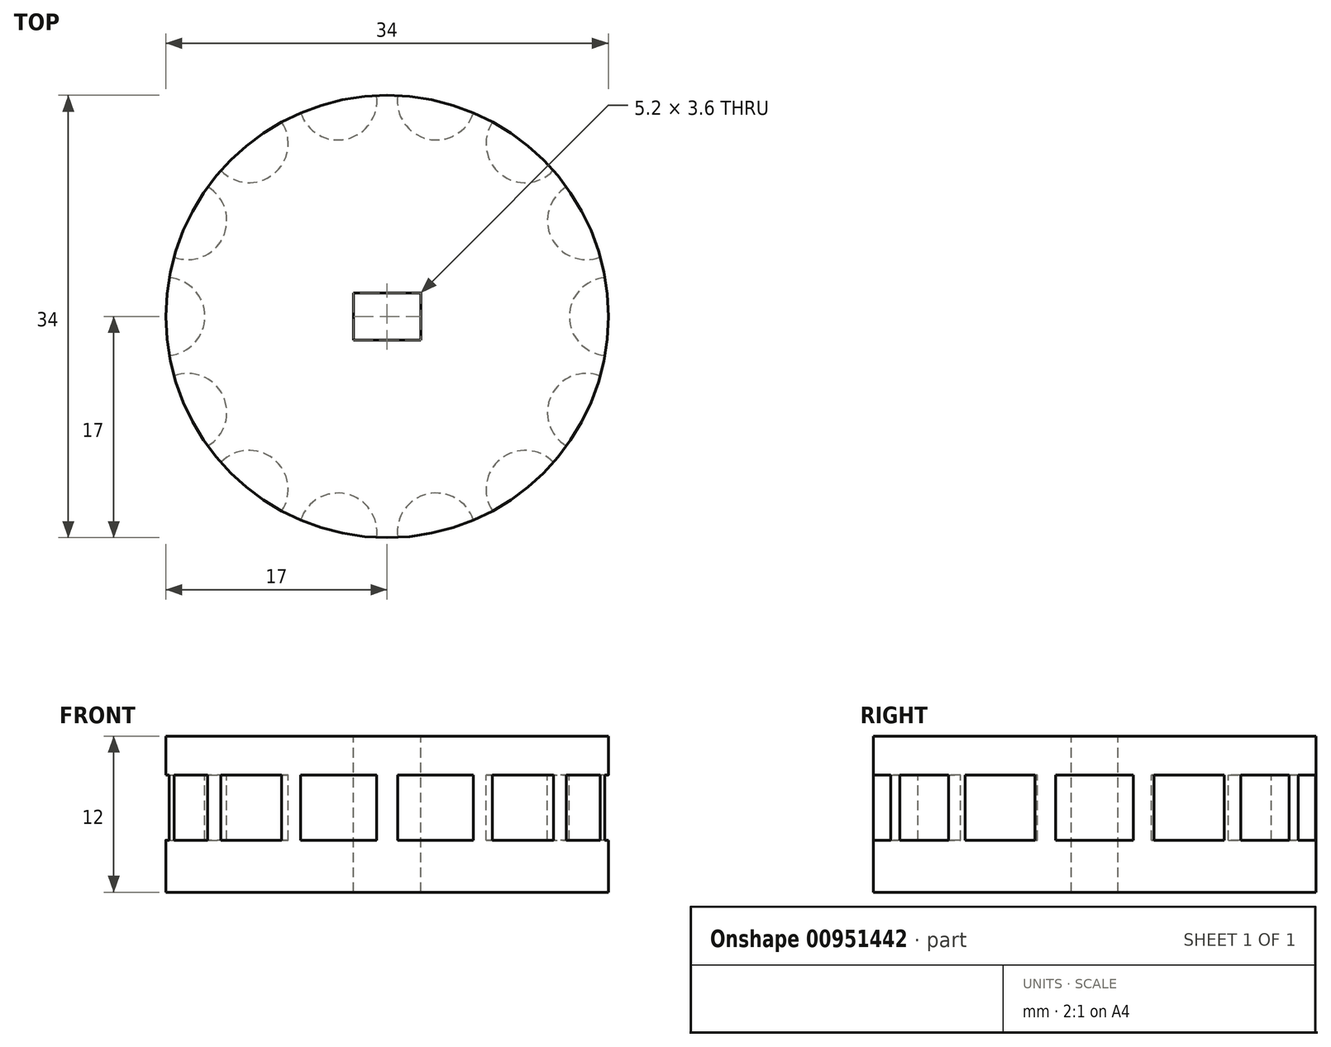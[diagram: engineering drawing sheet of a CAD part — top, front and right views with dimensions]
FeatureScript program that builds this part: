
annotation { "Feature Type Name" : "Feature", "Feature Type Description" : "" }
export const myFeature = defineFeature(function(context is Context, id is Id, definition is map)
    precondition{}
    {
        {
            var Q0;
            Q0=qCreatedBy(makeId("Top.planeOp"),FACE);
            var sketch = newSketch(context, id + "F0", { "sketchPlane" : qUnion([Q0])});
            skCircle(sketch, "E0", {"center": v(0, 0) * mm, "radius": 17 * mm});
            skSolve(sketch);
        }
        {
            var Q0;
            Q0=makeQuery(id+"F0.imprint","IMPRINT",FACE,{"disambiguationData":[TD([[makeQuery(id+"F0.imprint","IMPRINT",EDGE,{"derivedFrom":sQuery(id+"F0.wireOp",EDGE,"E0")}),1.0]])]});
            extrude(context, id + "F1", {"entities" : qUnion([Q0]), "depth" : 4 * mm, "offsetDistance" : 25 * mm});
        }
        {
            var Q0;
            Q0=makeQuery(id+"F1.opExtrude","CAP_FACE",FACE,{"disambiguationData":[OSD([sQuery(id+"F0.wireOp",EDGE,"E0")])],"isStart":false});
            var sketch = newSketch(context, id + "F2", { "sketchPlane" : qUnion([Q0])});
            skCircle(sketch, "E1", {"center": v(0, 0) * mm, "radius": 17 * mm});
            skSolve(sketch);
        }
        {
            var Q0;
            Q0=makeQuery(id+"F2.imprint","IMPRINT",FACE,{"disambiguationData":[TD([[makeQuery(id+"F2.imprint","IMPRINT",EDGE,{"derivedFrom":sQuery(id+"F2.wireOp",EDGE,"E1")}),1.0]])]});
            extrude(context, id + "F3", {"entities" : qUnion([Q0]), "operationType" : NewBodyOperationType.ADD, "depth" : 5 * mm, "offsetDistance" : 25 * mm});
        }
        {
            var Q0;
            Q0=makeQuery(id+"F3.opExtrude","CAP_FACE",FACE,{"disambiguationData":[OSD([sQuery(id+"F2.wireOp",EDGE,"E1")])],"isStart":false});
            var sketch = newSketch(context, id + "F4", { "sketchPlane" : qUnion([Q0])});
            skCircle(sketch, "E2", {"center": v(17, 0) * mm, "radius": 3 * mm});
            skLineSegment(sketch, "E3", {"start": v(17, 3) * mm, "end": v(19.07, 3) * mm});
            skLineSegment(sketch, "E4", {"start": v(17, -3) * mm, "end": v(19.07, -3) * mm});
            skLineSegment(sketch, "E5", {"start": v(19.07, -3) * mm, "end": v(19.07, 3) * mm});
            skSolve(sketch);
        }
        {
            var Q0;
            {var subQ0=sQuery(id+"F4.wireOp",EDGE,"E2");var subQ1=makeQuery(id+"F3.opExtrude","CAP_EDGE",EDGE,{"disambiguationData":[OSD([sQuery(id+"F2.wireOp",EDGE,"E1")])],"isStart":false});var subQ2=makeQuery(id+"F4.imprint","INTERSECT",VERTEX,{"disambiguationData":[OD(0.0)],"derivedFrom":[subQ1,subQ0]});Q0=makeQuery(id+"F4.imprint","IMPRINT",FACE,{"disambiguationData":[TD([[makeQuery(id+"F4.imprint","IMPRINT",EDGE,{"disambiguationData":[TD([[subQ2,1.0]])],"derivedFrom":subQ0}),1.0]])]});}
            var Q1;
            {var subQ0=sQuery(id+"F4.wireOp",EDGE,"E3");Q1=makeQuery(id+"F4.imprint","IMPRINT",FACE,{"disambiguationData":[TD([[makeQuery(id+"F4.imprint","IMPRINT",EDGE,{"derivedFrom":subQ0}),-1.0]])]});}
            var Q2;
            {var subQ0=sQuery(id+"F4.wireOp",EDGE,"E2");var subQ1=makeQuery(id+"F3.opExtrude","CAP_EDGE",EDGE,{"disambiguationData":[OSD([sQuery(id+"F2.wireOp",EDGE,"E1")])],"isStart":false});var subQ2=makeQuery(id+"F4.imprint","INTERSECT",VERTEX,{"disambiguationData":[OD(0.0)],"derivedFrom":[subQ1,subQ0]});Q2=makeQuery(id+"F4.imprint","IMPRINT",FACE,{"disambiguationData":[TD([[makeQuery(id+"F4.imprint","IMPRINT",EDGE,{"disambiguationData":[TD([[subQ2,-1.0]])],"derivedFrom":subQ0}),1.0]])]});}
            extrude(context, id + "F5", {"entities" : qUnion([Q0, Q1, Q2]), "oppositeDirection" : true, "depth" : 5 * mm, "offsetDistance" : 25 * mm});
        }
        {
            var Q0;
            Q0=makeQuery(id+"F5.opExtrude","SWEPT_BODY",BODY,{"disambiguationData":[OSD([sQuery(id+"F2.wireOp",EDGE,"E1"),sQuery(id+"F4.wireOp",EDGE,"E2")])]});
            var Q1;
            Q1=makeQuery(id+"F3.opExtrude","CAP_EDGE",EDGE,{"disambiguationData":[OSD([sQuery(id+"F2.wireOp",EDGE,"E1")])],"isStart":false});
            circularPattern(context, id + "F6", {"operationType" : NewBodyOperationType.REMOVE, "entities" : qUnion([Q0]), "axis" : qUnion([Q1]), "angle" : 360 * degree, "instanceCount" : 14, "equalSpace" : true});
        }
        {
            var Q0;
            Q0=makeQuery(id+"F3.opExtrude","CAP_FACE",FACE,{"disambiguationData":[OSD([sQuery(id+"F2.wireOp",EDGE,"E1")])],"isStart":false});
            var sketch = newSketch(context, id + "F7", { "sketchPlane" : qUnion([Q0])});
            skCircle(sketch, "E6", {"center": v(0, 0) * mm, "radius": 17 * mm});
            skSolve(sketch);
        }
        {
            var Q0;
            Q0 = qSketchRegion(id + "F7", true);
            extrude(context, id + "F8", {"entities" : qUnion([Q0]), "operationType" : NewBodyOperationType.ADD, "depth" : 3 * mm, "offsetDistance" : 25 * mm});
        }
        {
            var Q0;
            Q0=makeQuery(id+"F8.opExtrude","CAP_FACE",FACE,{"disambiguationData":[OSD([sQuery(id+"F7.wireOp",EDGE,"E6")])],"isStart":false});
            var sketch = newSketch(context, id + "F9", { "sketchPlane" : qUnion([Q0])});
            skLineSegment(sketch, "E7.bottom", {"start": v(2.6, 1.8) * mm, "end": v(-2.6, 1.8) * mm});
            skLineSegment(sketch, "E7.top", {"start": v(2.6, -1.8) * mm, "end": v(-2.6, -1.8) * mm});
            skLineSegment(sketch, "E7.left", {"start": v(2.6, 1.8) * mm, "end": v(2.6, -1.8) * mm});
            skLineSegment(sketch, "E7.right", {"start": v(-2.6, 1.8) * mm, "end": v(-2.6, -1.8) * mm});
            skPoint(sketch, "E7.middle", {"position": v(0, 0) * mm});
            skSolve(sketch);
        }
        {
            var Q0;
            Q0 = qSketchRegion(id + "F9", true);
            extrude(context, id + "F10", {"entities" : qUnion([Q0]), "operationType" : NewBodyOperationType.REMOVE, "oppositeDirection" : true, "depth" : 300 * mm, "offsetDistance" : 25 * mm});
        }
    });
